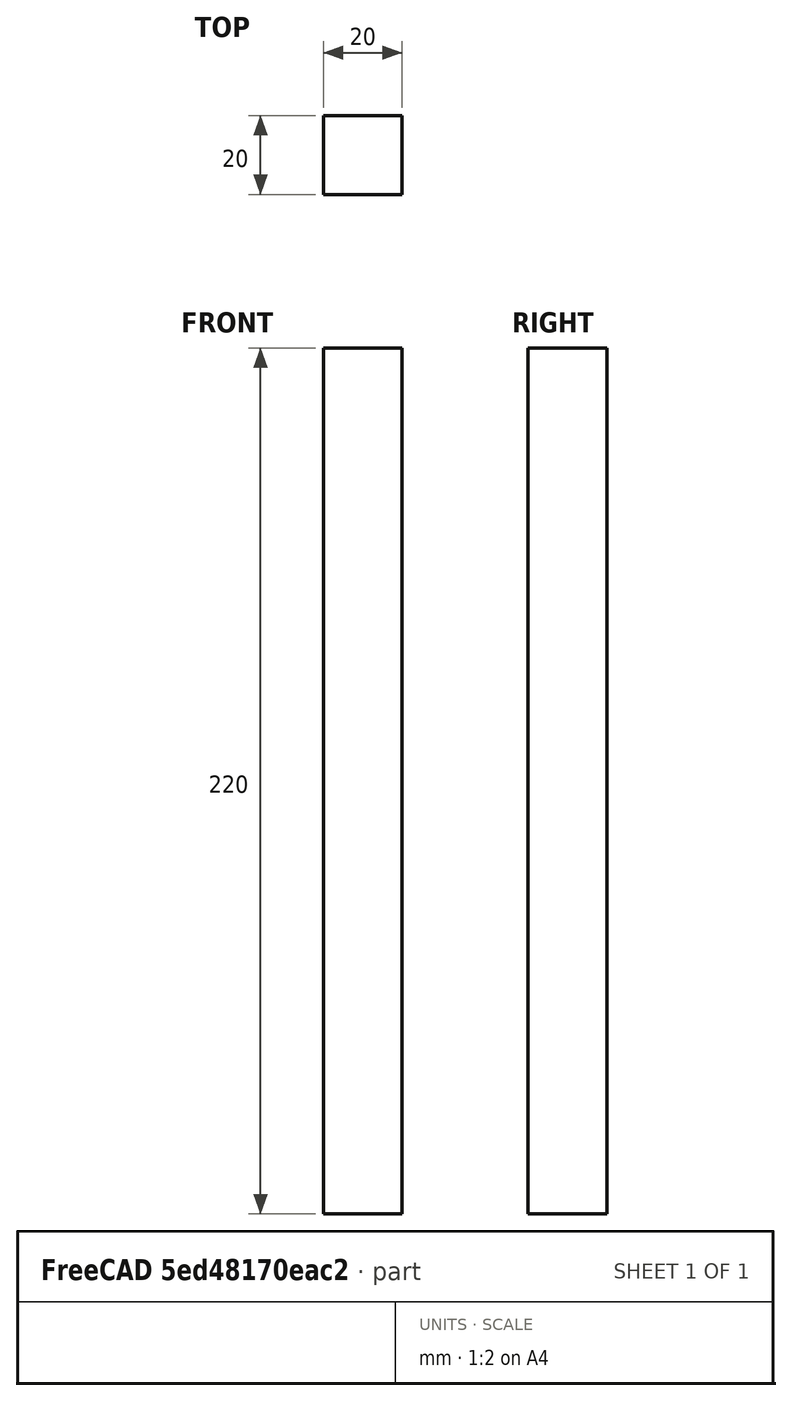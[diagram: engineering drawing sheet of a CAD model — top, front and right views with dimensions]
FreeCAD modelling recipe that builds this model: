
FCSTD DOCUMENT  (FreeCAD 0.19R24276 (Git))
Label: L220
License: All rights reserved
LicenseURL: http://en.wikipedia.org/wiki/All_rights_reserved
objects: Sketcher::SketchObject×1, PartDesign::Pad×1, PartDesign::Body×1
note: 4 computed .brp shape members not serialized (recipe doc carries the construction recipe); baked Part::Feature solids carry a one-line shape summary decoded from their .brp

FEATURE [Sketcher::SketchObject] Sketch
  FullyConstrained = true
  MapMode = 5
  Support = -> [XY_Plane]
  sketch-geometry (4):
    g0: LineSegment StartX=0 StartY=0 StartZ=0 EndX=20 EndY=0 EndZ=0
    g1: LineSegment StartX=20 StartY=0 StartZ=0 EndX=20 EndY=-20 EndZ=0
    g2: LineSegment StartX=20 StartY=-20 StartZ=0 EndX=0 EndY=-20 EndZ=0
    g3: LineSegment StartX=0 StartY=-20 StartZ=0 EndX=0 EndY=0 EndZ=0
  constraints (11):
    c: Coincident(g0,g1)
    c: Coincident(g1,g2)
    c: Coincident(g2,g3)
    c: Coincident(g3,g0)
    c: Horizontal(g0)
    c: Horizontal(g2)
    c: Vertical(g1)
    c: Vertical(g3)
    c: Coincident(g0,g-1)
    c: Equal(g1,g2)
    c: DistanceY(g1,g1) = 20
FEATURE [PartDesign::Pad] Pad
  Direction = (1,1,1)
  Length = 220
  Length2 = 100
  Profile = -> Sketch
  Type = 0
FEATURE [PartDesign::Body] Body
  Group = -> [Sketch,Pad]
  Origin = -> Origin
  Tip = -> Pad
